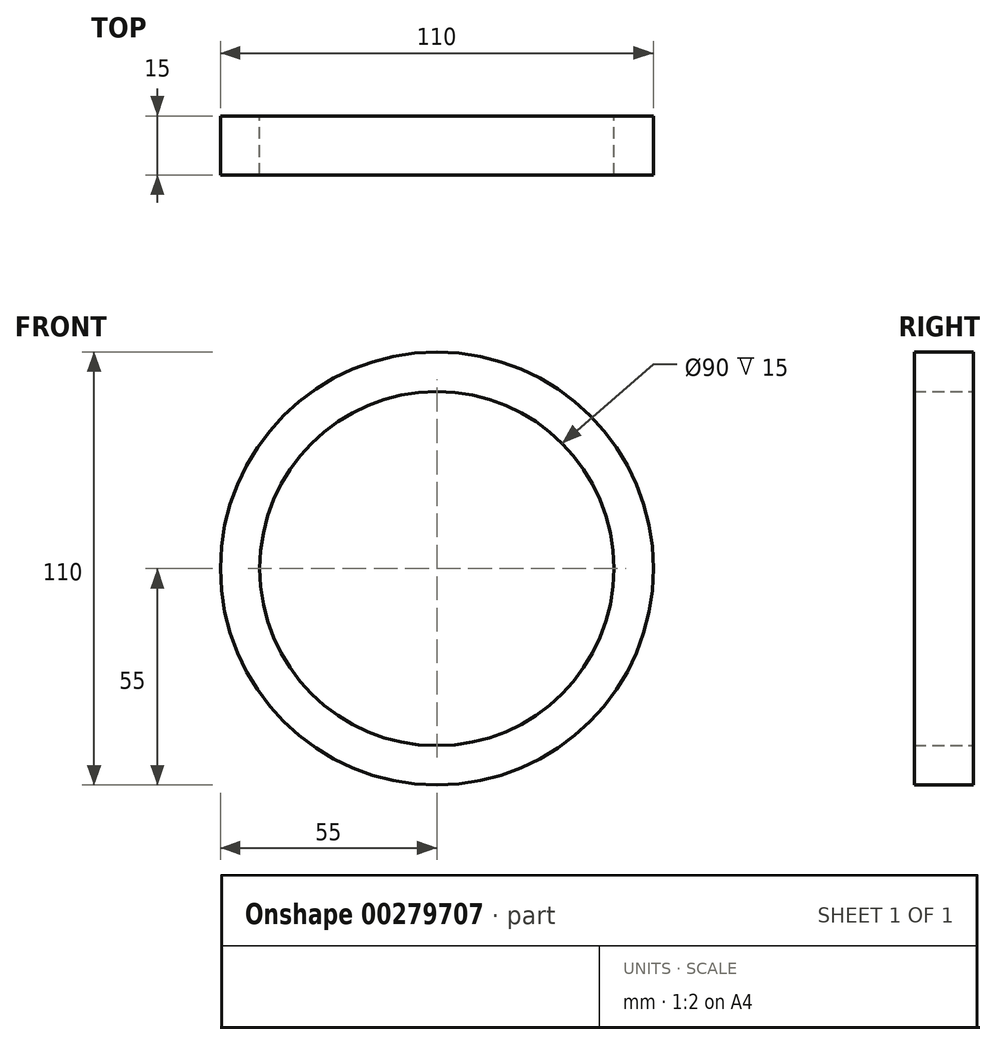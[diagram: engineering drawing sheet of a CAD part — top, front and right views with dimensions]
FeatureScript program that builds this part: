
annotation { "Feature Type Name" : "Feature", "Feature Type Description" : "" }
export const myFeature = defineFeature(function(context is Context, id is Id, definition is map)
    precondition{}
    {
        {
            var Q0;
            Q0=qCreatedBy(makeId("Front.planeOp"),FACE);
            var sketch = newSketch(context, id + "F0", { "sketchPlane" : qUnion([Q0])});
            skCircle(sketch, "E0", {"center": v(0, 0) * mm, "radius": 55 * mm});
            skCircle(sketch, "E1", {"center": v(0, 0) * mm, "radius": 45 * mm});
            skSolve(sketch);
        }
        {
            var Q0;
            Q0=makeQuery(id+"F0.imprint","IMPRINT",FACE,{"disambiguationData":[TD([[makeQuery(id+"F0.imprint","IMPRINT",EDGE,{"derivedFrom":sQuery(id+"F0.wireOp",EDGE,"E0")}),1.0]])]});
            extrude(context, id + "F1", {"entities" : qUnion([Q0]), "endBound" : BoundingType.SYMMETRIC, "depth" : 15 * mm});
        }
    });
